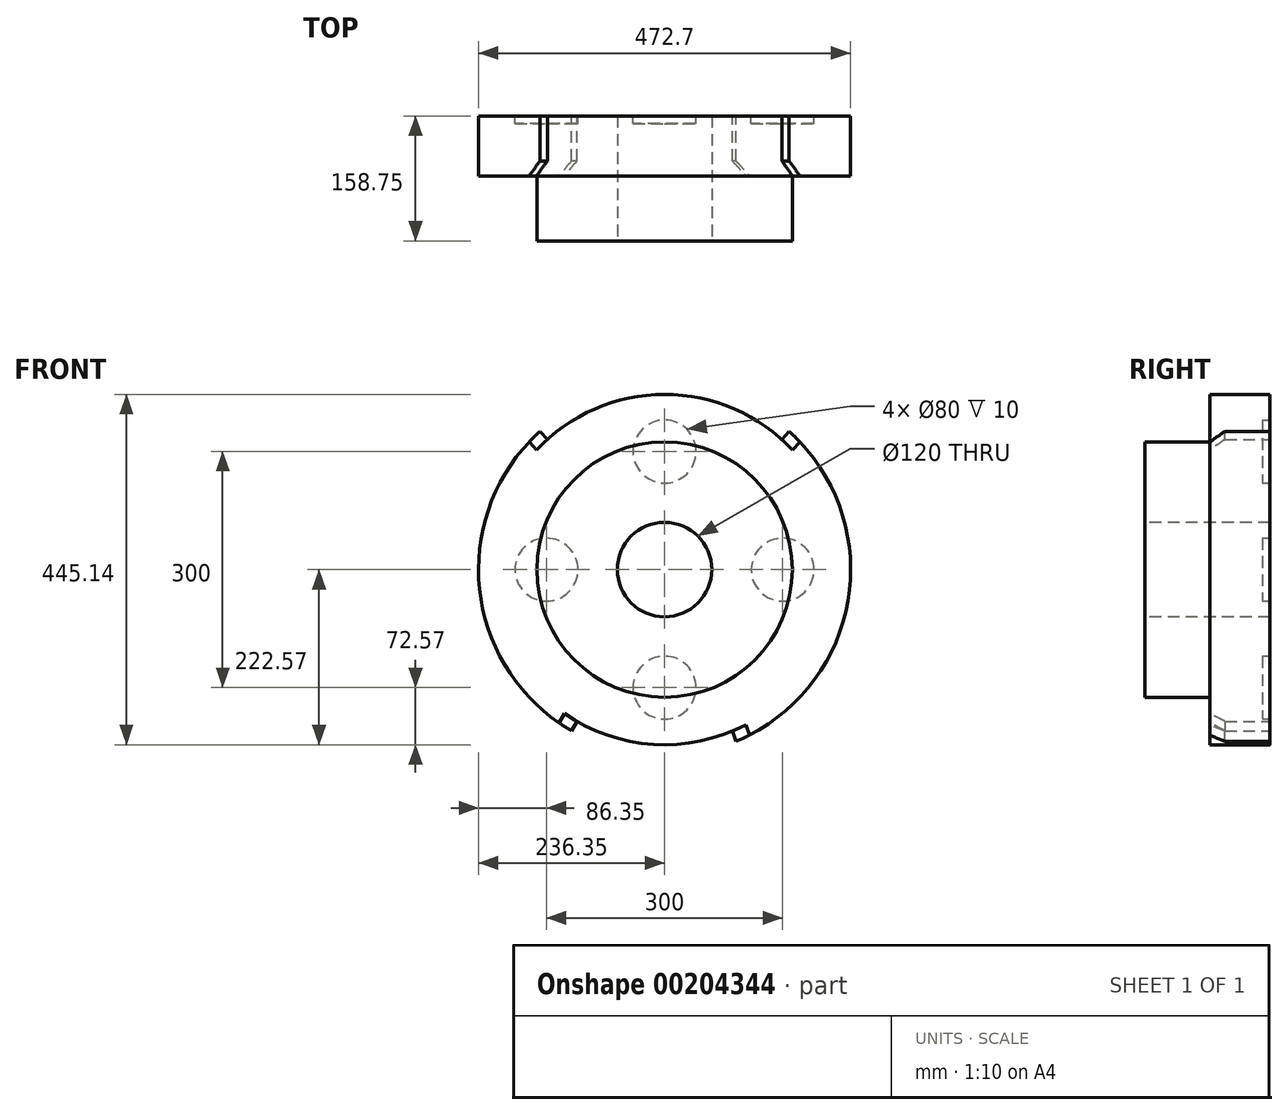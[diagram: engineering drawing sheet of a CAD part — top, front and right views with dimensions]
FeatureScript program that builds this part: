
annotation { "Feature Type Name" : "Feature", "Feature Type Description" : "" }
export const myFeature = defineFeature(function(context is Context, id is Id, definition is map)
    precondition{}
    {
        {
            var Q0;
            Q0=qCreatedBy(makeId("Front.planeOp"),FACE);
            var sketch = newSketch(context, id + "F0", { "sketchPlane" : qUnion([Q0])});
            skCircle(sketch, "E0", {"center": v(0, 0) * mm, "radius": 236.35 * mm});
            skSolve(sketch);
        }
        {
            var Q0;
            Q0 = qSketchRegion(id + "F0", true);
            extrude(context, id + "F1", {"entities" : qUnion([Q0]), "depth" : 76.2 * mm});
        }
        {
            var Q0;
            Q0=makeQuery(id+"F1.opExtrude","CAP_FACE",FACE,{"disambiguationData":[OSD([sQuery(id+"F0.wireOp",EDGE,"E0")])],"isStart":false});
            var sketch = newSketch(context, id + "F2", { "sketchPlane" : qUnion([Q0])});
            skCircle(sketch, "E1", {"center": v(0, 0) * mm, "radius": 162.18 * mm});
            skSolve(sketch);
        }
        {
            var Q0;
            Q0 = qSketchRegion(id + "F2", true);
            extrude(context, id + "F3", {"entities" : qUnion([Q0]), "operationType" : NewBodyOperationType.ADD, "depth" : 82.55 * mm});
        }
        {
            var Q0;
            Q0=makeQuery(id+"F1.opExtrude","CAP_FACE",FACE,{"disambiguationData":[OSD([sQuery(id+"F0.wireOp",EDGE,"E0")])],"isStart":true});
            var sketch = newSketch(context, id + "F4", { "sketchPlane" : qUnion([Q0])});
            skLineSegment(sketch, "E2", {"start": v(-148.93, 165.4) * mm, "end": v(-184.81, 205.26) * mm});
            skLineSegment(sketch, "E3", {"start": v(111.28, -192.75) * mm, "end": v(138.95, -240.67) * mm});
            skLineSegment(sketch, "E4", {"start": v(148.93, 165.4) * mm, "end": v(183.39, 203.67) * mm});
            skLineSegment(sketch, "E5", {"start": v(-86.04, -205.26) * mm, "end": v(-123.6, -308.45) * mm});
            skLineSegment(sketch, "E6", {"start": v(-184.81, 205.26) * mm, "end": v(0, 288.64) * mm});
            skLineSegment(sketch, "E7", {"start": v(0, 288.64) * mm, "end": v(183.39, 203.67) * mm});
            skLineSegment(sketch, "E8", {"start": v(138.95, -240.67) * mm, "end": v(23.06, -307.59) * mm});
            skLineSegment(sketch, "E9", {"start": v(23.06, -307.59) * mm, "end": v(-123.6, -308.45) * mm});
            skPoint(sketch, "E10.orphan", {"position": v(-11.33, 0) * mm});
            skArc(sketch, "E11.trimOffspring", {"start": v(-86.04, -205.26) * mm, "mid": v(14.09, -222.12) * mm, "end": v(111.28, -192.75) * mm});
            skArc(sketch, "E12", {"start": v(148.93, 165.4) * mm, "mid": v(0, 222.57) * mm, "end": v(-148.93, 165.4) * mm});
            skSolve(sketch);
        }
        {
            var Q0;
            Q0 = qSketchRegion(id + "F4", true);
            extrude(context, id + "F5", {"entities" : qUnion([Q0]), "operationType" : NewBodyOperationType.REMOVE, "oppositeDirection" : true, "depth" : 139.7 * mm});
        }
        {
            var Q0;
            Q0=makeQuery(id+"F5.boolean.opBoolean","INTERSECT",EDGE,{"derivedFrom":[makeQuery(id+"F1.opExtrude","CAP_FACE",FACE,{"disambiguationData":[OSD([sQuery(id+"F0.wireOp",EDGE,"E0")])],"isStart":false}),makeQuery(id+"F5.opExtrude","SWEPT_FACE",FACE,{"disambiguationData":[OSD([sQuery(id+"F4.wireOp",EDGE,"E5")])]})]});
            chamfer(context, id + "F6", {"entities" : qUnion([Q0]), "width" : 19.05 * mm, "tangentPropagation" : true});
        }
        {
            var Q0;
            Q0=makeQuery(id+"F5.boolean.opBoolean","INTERSECT",EDGE,{"derivedFrom":[makeQuery(id+"F1.opExtrude","CAP_FACE",FACE,{"disambiguationData":[OSD([sQuery(id+"F0.wireOp",EDGE,"E0")])],"isStart":false}),makeQuery(id+"F5.opExtrude","SWEPT_FACE",FACE,{"disambiguationData":[OSD([sQuery(id+"F4.wireOp",EDGE,"E3")])]})]});
            chamfer(context, id + "F7", {"entities" : qUnion([Q0]), "width" : 19.05 * mm, "tangentPropagation" : true});
        }
        {
            var Q0;
            Q0=makeQuery(id+"F5.boolean.opBoolean","INTERSECT",EDGE,{"derivedFrom":[makeQuery(id+"F1.opExtrude","CAP_FACE",FACE,{"disambiguationData":[OSD([sQuery(id+"F0.wireOp",EDGE,"E0")])],"isStart":false}),makeQuery(id+"F5.opExtrude","SWEPT_FACE",FACE,{"disambiguationData":[OSD([sQuery(id+"F4.wireOp",EDGE,"E2")])]})]});
            chamfer(context, id + "F8", {"entities" : qUnion([Q0]), "width" : 19.05 * mm, "tangentPropagation" : true});
        }
        {
            var Q0;
            Q0=makeQuery(id+"F5.boolean.opBoolean","INTERSECT",EDGE,{"derivedFrom":[makeQuery(id+"F1.opExtrude","CAP_FACE",FACE,{"disambiguationData":[OSD([sQuery(id+"F0.wireOp",EDGE,"E0")])],"isStart":false}),makeQuery(id+"F5.opExtrude","SWEPT_FACE",FACE,{"disambiguationData":[OSD([sQuery(id+"F4.wireOp",EDGE,"E4")])]})]});
            chamfer(context, id + "F9", {"entities" : qUnion([Q0]), "width" : 19.05 * mm, "tangentPropagation" : true});
        }
        {
            var Q0;
            Q0=makeQuery(id+"F1.opExtrude","CAP_FACE",FACE,{"disambiguationData":[OSD([sQuery(id+"F0.wireOp",EDGE,"E0")])],"isStart":true});
            var sketch = newSketch(context, id + "F10", { "sketchPlane" : qUnion([Q0])});
            skCircle(sketch, "E13", {"center": v(0, 150) * mm, "radius": 40 * mm});
            skCircle(sketch, "E14.1.0", {"center": v(-150, 0) * mm, "radius": 40 * mm});
            skCircle(sketch, "E14.2.0", {"center": v(0, -150) * mm, "radius": 40 * mm});
            skCircle(sketch, "E14.3.0", {"center": v(150, 0) * mm, "radius": 40 * mm});
            skPoint(sketch, "E14.center", {"position": v(0, 0) * mm});
            skSolve(sketch);
        }
        {
            var Q0;
            Q0 = qSketchRegion(id + "F10", true);
            extrude(context, id + "F11", {"entities" : qUnion([Q0]), "operationType" : NewBodyOperationType.REMOVE, "oppositeDirection" : true, "depth" : 10 * mm});
        }
        {
            var Q0;
            Q0=makeQuery(id+"F3.opExtrude","CAP_FACE",FACE,{"disambiguationData":[OSD([sQuery(id+"F2.wireOp",EDGE,"E1")])],"isStart":false});
            var sketch = newSketch(context, id + "F12", { "sketchPlane" : qUnion([Q0])});
            skCircle(sketch, "E15", {"center": v(0, 0) * mm, "radius": 60 * mm});
            skSolve(sketch);
        }
        {
            var Q0;
            Q0 = qSketchRegion(id + "F12", true);
            extrude(context, id + "F13", {"entities" : qUnion([Q0]), "operationType" : NewBodyOperationType.REMOVE, "oppositeDirection" : true, "depth" : 550 * mm});
        }
    });
